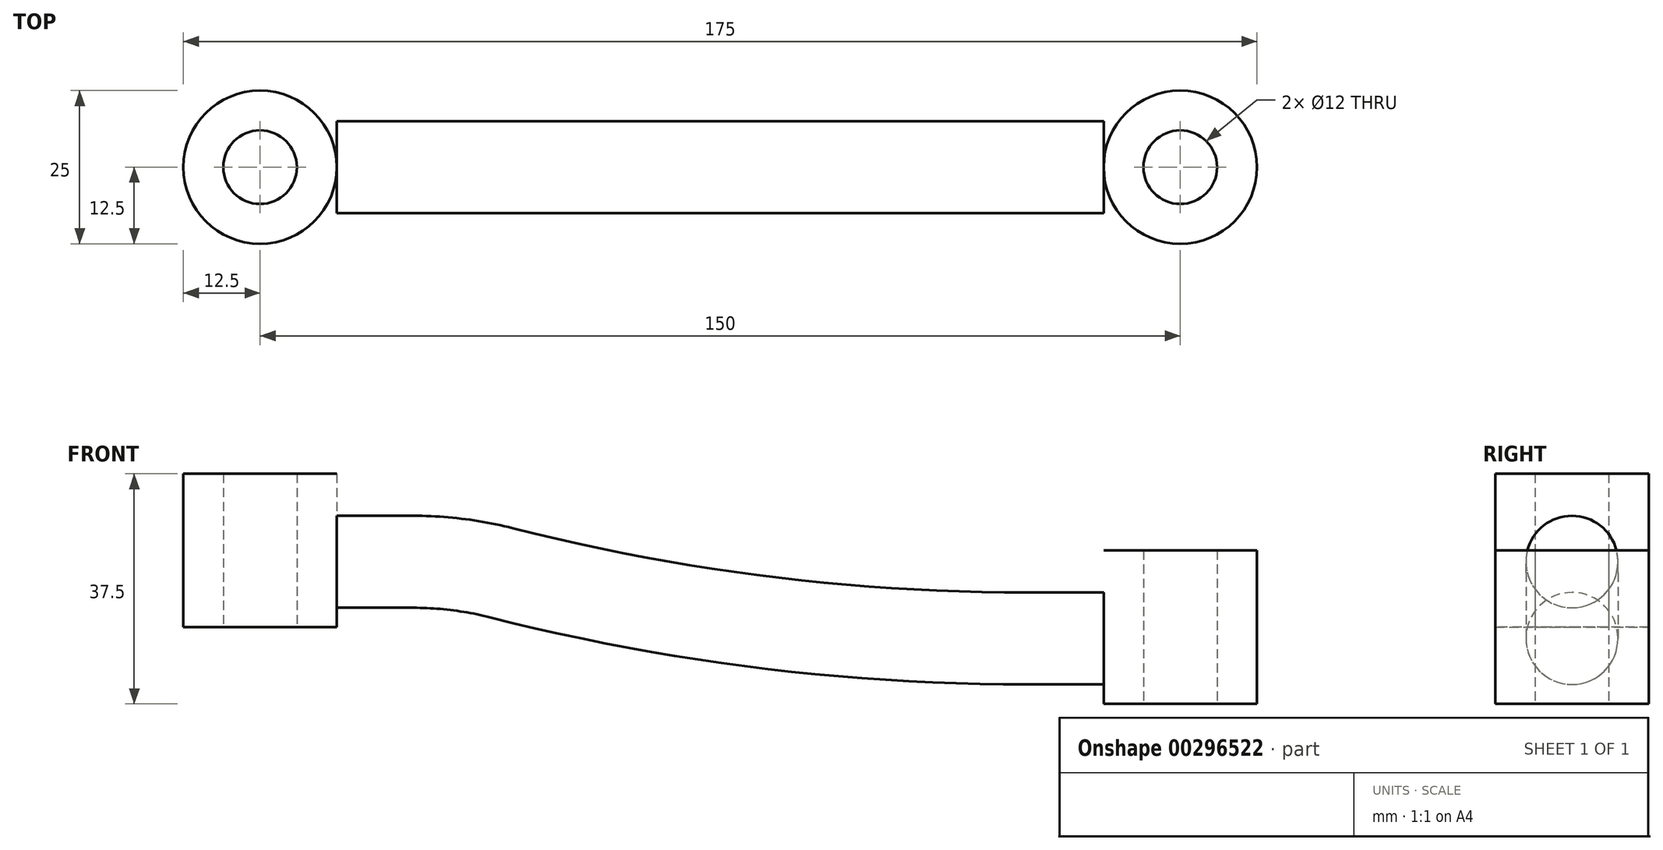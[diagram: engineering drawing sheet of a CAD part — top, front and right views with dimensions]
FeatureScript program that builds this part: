
annotation { "Feature Type Name" : "Feature", "Feature Type Description" : "" }
export const myFeature = defineFeature(function(context is Context, id is Id, definition is map)
    precondition{}
    {
        {
            var Q0;
            Q0=qCreatedBy(makeId("Top.planeOp"),FACE);
            var sketch = newSketch(context, id + "F0", { "sketchPlane" : qUnion([Q0])});
            skCircle(sketch, "E0", {"center": v(0, 0) * mm, "radius": 12.5 * mm});
            skCircle(sketch, "E1", {"center": v(74.73, 0) * mm, "radius": 12.5 * mm});
            skCircle(sketch, "E2", {"center": v(0, 0) * mm, "radius": 6 * mm});
            skSolve(sketch);
        }
        {
            var Q0;
            Q0=makeQuery(id+"F0.imprint","IMPRINT",FACE,{"disambiguationData":[TD([[makeQuery(id+"F0.imprint","IMPRINT",EDGE,{"derivedFrom":sQuery(id+"F0.wireOp",EDGE,"E0")}),1.0]])]});
            extrude(context, id + "F1", {"entities" : qUnion([Q0]), "depth" : 25 * mm});
        }
        {
            var Q0;
            Q0=qCreatedBy(makeId("Top.planeOp"),FACE);
            var sketch = newSketch(context, id + "F2", { "sketchPlane" : qUnion([Q0])});
            skCircle(sketch, "E3", {"center": v(150, 0) * mm, "radius": 12.5 * mm});
            skCircle(sketch, "E4", {"center": v(150, 0) * mm, "radius": 6 * mm});
            skSolve(sketch);
        }
        {
            var Q0;
            Q0 = qSketchRegion(id + "F2", true);
            extrude(context, id + "F3", {"entities" : qUnion([Q0]), "endBound" : BoundingType.SYMMETRIC, "depth" : 25 * mm});
        }
        {
            var Q0;
            Q0=qCreatedBy(makeId("Front.planeOp"),FACE);
            var sketch = newSketch(context, id + "F4", { "sketchPlane" : qUnion([Q0])});
            skLineSegment(sketch, "E5", {"start": v(12.5, 12.5) * mm, "end": v(25, 12.5) * mm});
            skArc(sketch, "E6", {"start": v(25, 12.5) * mm, "mid": v(32.44, 12.04) * mm, "end": v(39.77, 10.65) * mm});
            skArc(sketch, "E7", {"start": v(39.77, 10.65) * mm, "mid": v(82.05, 2.67) * mm, "end": v(125, 0) * mm});
            skLineSegment(sketch, "E8", {"start": v(125, 0) * mm, "end": v(137.5, 0) * mm});
            skSolve(sketch);
        }
        {
            var Q0;
            Q0=qCreatedBy(makeId("Right.planeOp"),FACE);
            cPlane(context, id + "F5", {"entities" : qUnion([Q0]), "cplaneType" : CPlaneType.OFFSET, "offset" : 12.5 * mm, "width" : 150 * mm, "height" : 150 * mm});
        }
        {
            var Q0;
            Q0=qCreatedBy(id+"F5.planeOp",FACE);
            var sketch = newSketch(context, id + "F6", { "sketchPlane" : qUnion([Q0])});
            skCircle(sketch, "E9", {"center": v(0, 10.65) * mm, "radius": 7.5 * mm});
            skSolve(sketch);
        }
        {
            var Q0;
            Q0 = qSketchRegion(id + "F6", true);
            var Q1;
            Q1 = qConstructionFilter(qBodyType(qCreatedBy(id + "F4" ,EDGE), BodyType.WIRE), ConstructionObject.NO);
            sweep(context, id + "F7", {"profiles" : qUnion([Q0]), "path" : qUnion([Q1])});
        }
    });
